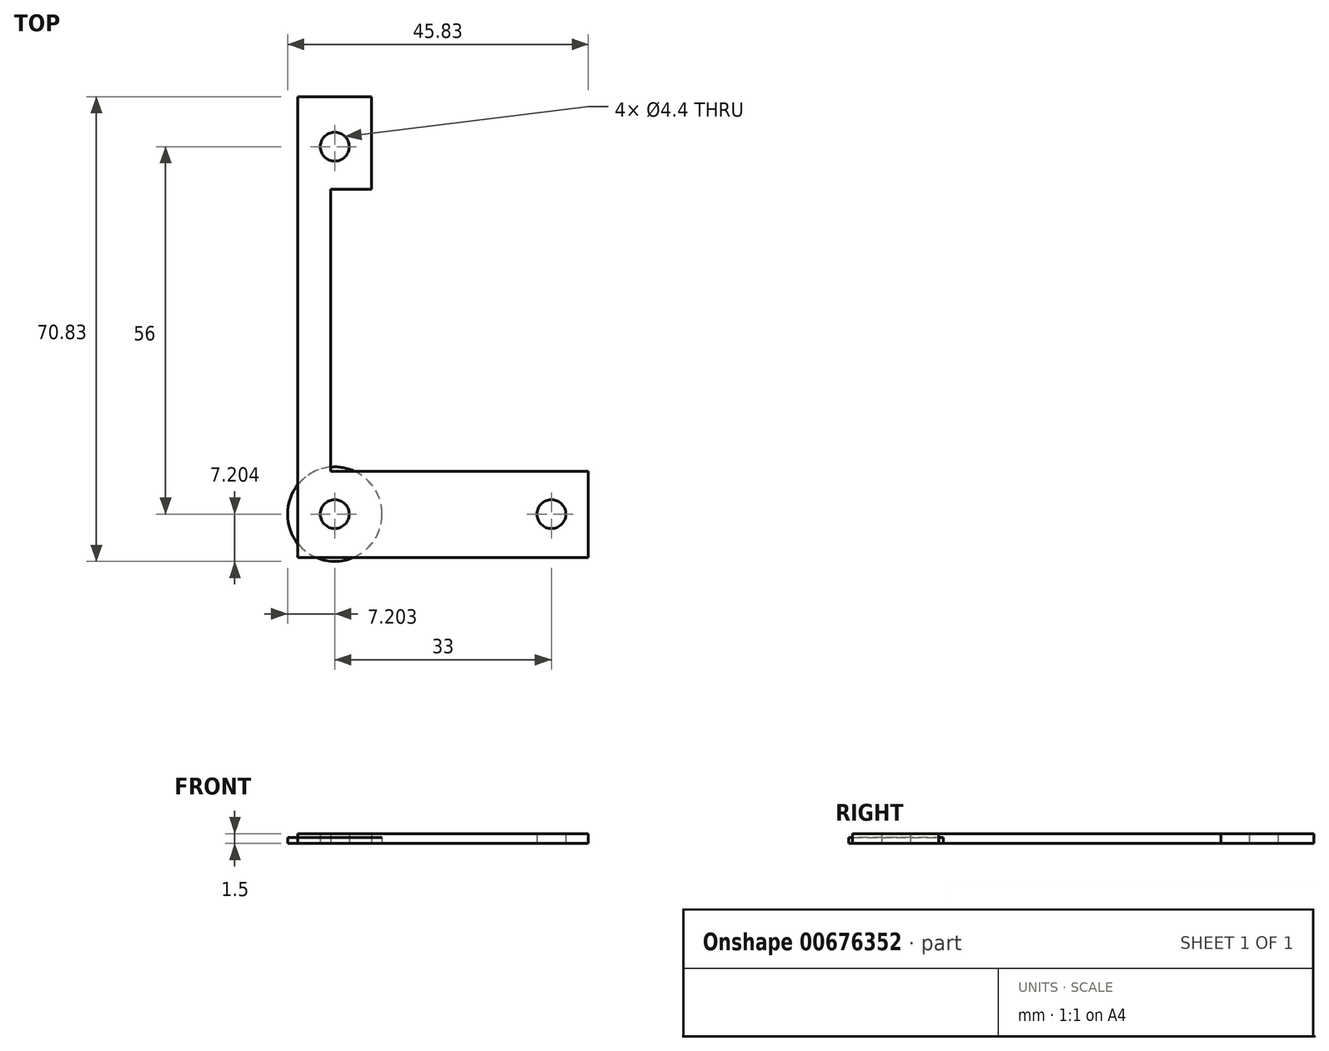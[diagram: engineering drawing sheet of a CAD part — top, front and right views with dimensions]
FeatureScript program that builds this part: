
annotation { "Feature Type Name" : "Feature", "Feature Type Description" : "" }
export const myFeature = defineFeature(function(context is Context, id is Id, definition is map)
    precondition{}
    {
        {
            var Q0;
            Q0=qCreatedBy(makeId("Top.planeOp"),FACE);
            var sketch = newSketch(context, id + "F0", { "sketchPlane" : qUnion([Q0])});
            skLineSegment(sketch, "E0", {"start": v(-31.24, 29.2) * mm, "end": v(-31.24, -41.05) * mm});
            skLineSegment(sketch, "E1", {"start": v(-31.24, -41.05) * mm, "end": v(13, -41.05) * mm});
            skLineSegment(sketch, "E2", {"start": v(13, -41.05) * mm, "end": v(13, -27.93) * mm});
            skLineSegment(sketch, "E3", {"start": v(13, -27.93) * mm, "end": v(-26.24, -27.93) * mm});
            skLineSegment(sketch, "E4", {"start": v(-26.24, -27.93) * mm, "end": v(-26.24, 15.07) * mm});
            skLineSegment(sketch, "E5", {"start": v(-26.24, 15.07) * mm, "end": v(-20, 15.07) * mm});
            skLineSegment(sketch, "E6", {"start": v(-20, 15.07) * mm, "end": v(-20, 29.2) * mm});
            skLineSegment(sketch, "E7", {"start": v(-20, 29.2) * mm, "end": v(-31.24, 29.2) * mm});
            skCircle(sketch, "E8", {"center": v(-25.62, -34.43) * mm, "radius": 2.2 * mm});
            skCircle(sketch, "E9", {"center": v(7.38, -34.43) * mm, "radius": 2.2 * mm});
            skCircle(sketch, "E10", {"center": v(-25.62, 21.57) * mm, "radius": 2.2 * mm});
            skSolve(sketch);
        }
        {
            var Q0;
            Q0=makeQuery(id+"F0.imprint","IMPRINT",FACE,{"disambiguationData":[TD([[makeQuery(id+"F0.imprint","IMPRINT",EDGE,{"derivedFrom":sQuery(id+"F0.wireOp",EDGE,"E0")}),1.0]])]});
            extrude(context, id + "F1", {"entities" : qUnion([Q0]), "depth" : 1.5 * mm, "offsetDistance" : 25 * mm});
        }
        {
            var Q0;
            Q0=qCreatedBy(makeId("Top.planeOp"),FACE);
            var sketch = newSketch(context, id + "F2", { "sketchPlane" : qUnion([Q0])});
            skCircle(sketch, "E11.0", {"center": v(-25.62, 21.57) * mm, "radius": 2.2 * mm});
            skCircle(sketch, "E12.0", {"center": v(-25.62, -34.43) * mm, "radius": 2.2 * mm});
            skCircle(sketch, "E13.0", {"center": v(7.38, -34.43) * mm, "radius": 2.2 * mm});
            skCircle(sketch, "E14.0", {"center": v(-25.62, 21.57) * mm, "radius": 7.2 * mm});
            skCircle(sketch, "E15.0", {"center": v(-25.62, -34.43) * mm, "radius": 7.2 * mm});
            skCircle(sketch, "E16.0", {"center": v(7.38, -34.43) * mm, "radius": 7.2 * mm});
            skSolve(sketch);
        }
        {
            var Q0;
            Q0=makeQuery(id+"F2.imprint","IMPRINT",FACE,{"disambiguationData":[TD([[makeQuery(id+"F2.imprint","IMPRINT",EDGE,{"derivedFrom":sQuery(id+"F2.wireOp",EDGE,"E12.0")}),-1.0]])]});
            extrude(context, id + "F3", {"entities" : qUnion([Q0]), "depth" : 0.9 * mm, "offsetDistance" : 25 * mm});
        }
    });
